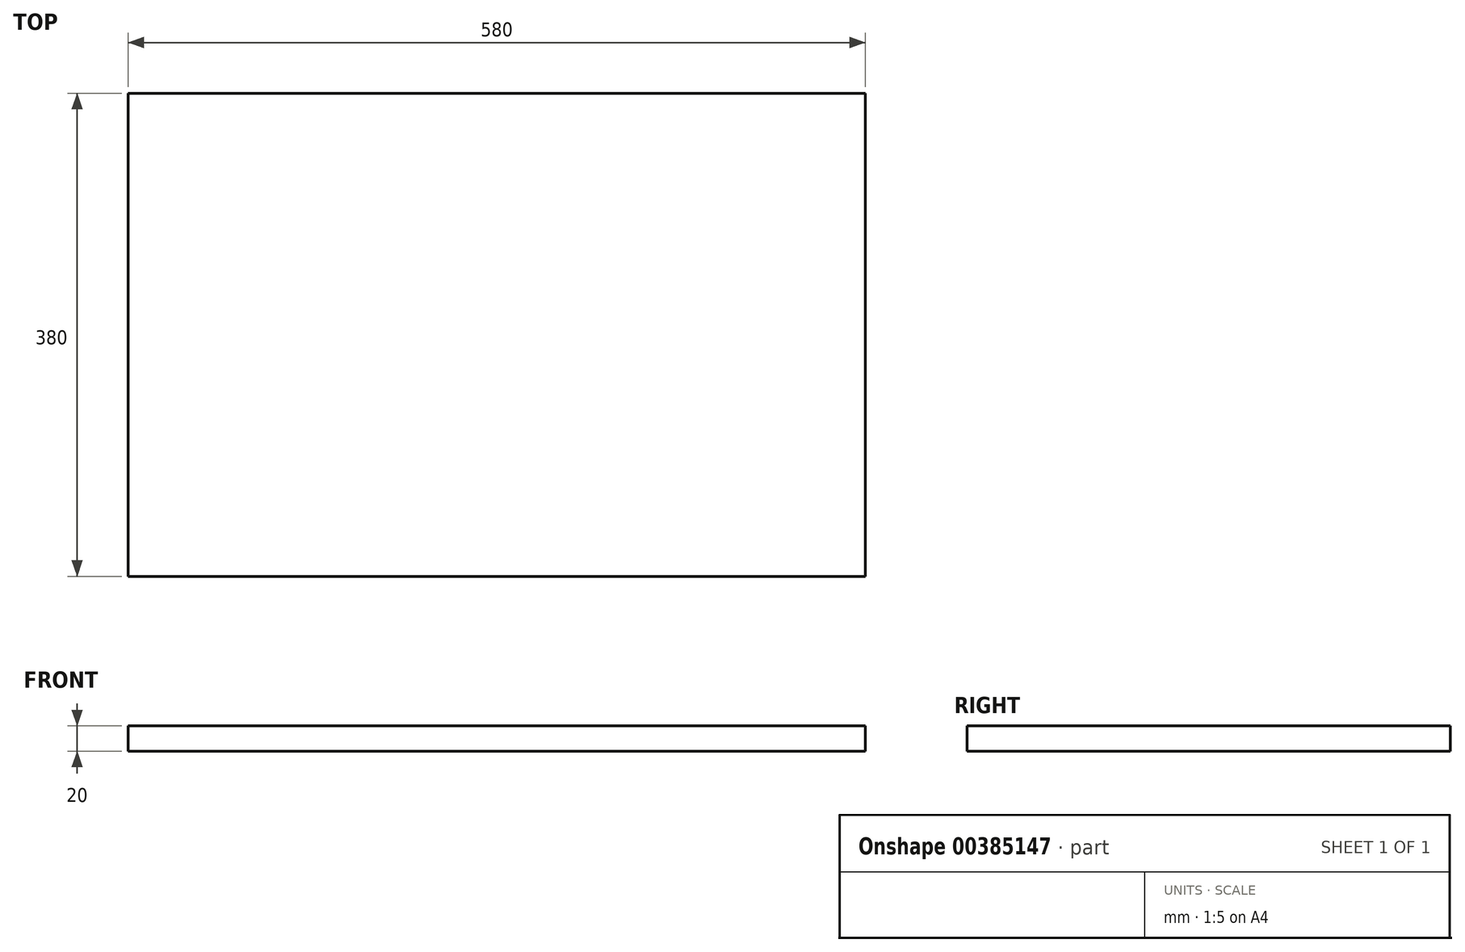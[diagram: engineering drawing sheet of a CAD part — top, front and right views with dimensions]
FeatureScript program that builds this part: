
annotation { "Feature Type Name" : "Feature", "Feature Type Description" : "" }
export const myFeature = defineFeature(function(context is Context, id is Id, definition is map)
    precondition{}
    {
        {
            var Q0;
            Q0=qCreatedBy(makeId("Top.planeOp"),FACE);
            var sketch = newSketch(context, id + "F0", { "sketchPlane" : qUnion([Q0])});
            skLineSegment(sketch, "E0.bottom", {"start": v(290, 190) * mm, "end": v(-290, 190) * mm});
            skLineSegment(sketch, "E0.top", {"start": v(290, -190) * mm, "end": v(-290, -190) * mm});
            skLineSegment(sketch, "E0.left", {"start": v(290, 190) * mm, "end": v(290, -190) * mm});
            skLineSegment(sketch, "E0.right", {"start": v(-290, 190) * mm, "end": v(-290, -190) * mm});
            skPoint(sketch, "E0.middle", {"position": v(0, 0) * mm});
            skSolve(sketch);
        }
        {
            var Q0;
            Q0=makeQuery(id+"F0.imprint","IMPRINT",FACE,{"disambiguationData":[TD([[makeQuery(id+"F0.imprint","IMPRINT",EDGE,{"derivedFrom":sQuery(id+"F0.wireOp",EDGE,"E0.bottom")}),1.0]])]});
            extrude(context, id + "F1", {"entities" : qUnion([Q0]), "depth" : 20 * mm});
        }
    });
